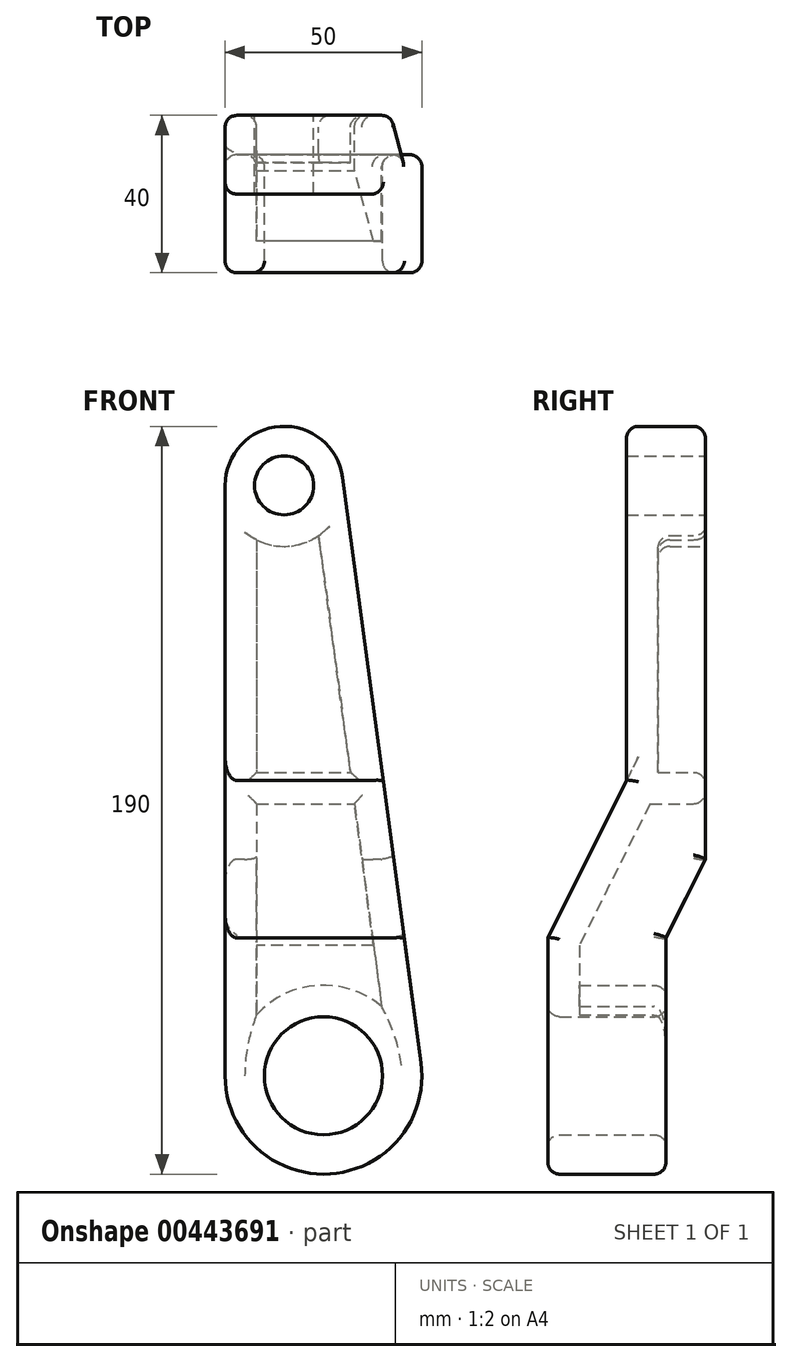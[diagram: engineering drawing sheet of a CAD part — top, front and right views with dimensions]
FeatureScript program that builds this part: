
annotation { "Feature Type Name" : "Feature", "Feature Type Description" : "" }
export const myFeature = defineFeature(function(context is Context, id is Id, definition is map)
    precondition{}
    {
        {
            var Q0;
            Q0=qCreatedBy(makeId("Front.planeOp"),FACE);
            var sketch = newSketch(context, id + "F0", { "sketchPlane" : qUnion([Q0])});
            skCircle(sketch, "E0", {"center": v(0, 0) * mm, "radius": 25 * mm});
            skCircle(sketch, "E1", {"center": v(-10, 150) * mm, "radius": 15 * mm});
            skLineSegment(sketch, "E2", {"start": v(-25, 150) * mm, "end": v(-25, 0) * mm});
            skLineSegment(sketch, "E3", {"start": v(4.87, 152) * mm, "end": v(24.78, 3.32) * mm});
            skSolve(sketch);
        }
        {
            var Q0;
            Q0 = qSketchRegion(id + "F0", true);
            extrude(context, id + "F1", {"entities" : qUnion([Q0]), "depth" : 40 * mm});
        }
        {
            var Q0;
            Q0=makeQuery(id+"F1.opExtrude","SWEPT_FACE",FACE,{"disambiguationData":[OSD([sQuery(id+"F0.wireOp",EDGE,"E2")])]});
            var sketch = newSketch(context, id + "F2", { "sketchPlane" : qUnion([Q0])});
            skLineSegment(sketch, "E4", {"start": v(0, 0) * mm, "end": v(0, -25.94) * mm});
            skLineSegment(sketch, "E5", {"start": v(10, -25.94) * mm, "end": v(10, 35) * mm});
            skLineSegment(sketch, "E6", {"start": v(10, 35) * mm, "end": v(0, 55) * mm});
            skLineSegment(sketch, "E7", {"start": v(0, 55) * mm, "end": v(0, -25.94) * mm});
            skLineSegment(sketch, "E8", {"start": v(40, 35) * mm, "end": v(40, 165.97) * mm});
            skLineSegment(sketch, "E9", {"start": v(20, 165.97) * mm, "end": v(20, 75) * mm});
            skLineSegment(sketch, "E10", {"start": v(20, 75) * mm, "end": v(40, 35) * mm});
            skLineSegment(sketch, "E11", {"start": v(0, -25.94) * mm, "end": v(10, -25.94) * mm});
            skLineSegment(sketch, "E12", {"start": v(20, 165.97) * mm, "end": v(40, 165.97) * mm});
            skSolve(sketch);
        }
        {
            var Q0;
            Q0 = qSketchRegion(id + "F2", true);
            extrude(context, id + "F3", {"entities" : qUnion([Q0]), "operationType" : NewBodyOperationType.REMOVE, "endBound" : BoundingType.THROUGH_ALL, "oppositeDirection" : true, "depth" : 25 * mm});
        }
        {
            var Q0;
            Q0=makeQuery(id+"F1.opExtrude","CAP_FACE",FACE,{"disambiguationData":[OSD([sQuery(id+"F0.wireOp",EDGE,"E0"),sQuery(id+"F0.wireOp",EDGE,"E1"),sQuery(id+"F0.wireOp",EDGE,"E2"),sQuery(id+"F0.wireOp",EDGE,"E3")])],"isStart":true});
            var sketch = newSketch(context, id + "F4", { "sketchPlane" : qUnion([Q0])});
            skCircle(sketch, "E13", {"center": v(10, 150) * mm, "radius": 7.5 * mm});
            skCircle(sketch, "E14", {"center": v(0, 0) * mm, "radius": 15 * mm});
            skSolve(sketch);
        }
        {
            var Q0;
            Q0 = qSketchRegion(id + "F4", true);
            extrude(context, id + "F5", {"entities" : qUnion([Q0]), "operationType" : NewBodyOperationType.REMOVE, "endBound" : BoundingType.THROUGH_ALL, "oppositeDirection" : true, "depth" : 25 * mm});
        }
        {
            var Q0;
            Q0=makeQuery(id+"F1.opExtrude","CAP_FACE",FACE,{"disambiguationData":[OSD([sQuery(id+"F0.wireOp",EDGE,"E0"),sQuery(id+"F0.wireOp",EDGE,"E1"),sQuery(id+"F0.wireOp",EDGE,"E2"),sQuery(id+"F0.wireOp",EDGE,"E3")])],"isStart":true});
            var Q1;
            Q1=makeQuery(id+"F3.boolean.opBoolean","COPY",FACE,{"derivedFrom":makeQuery(id+"F3.opExtrude","SWEPT_FACE",FACE,{"disambiguationData":[OSD([sQuery(id+"F2.wireOp",EDGE,"E6")])]})});
            var Q2;
            Q2=makeQuery(id+"F3.boolean.opBoolean","COPY",FACE,{"derivedFrom":makeQuery(id+"F3.opExtrude","SWEPT_FACE",FACE,{"disambiguationData":[OSD([sQuery(id+"F2.wireOp",EDGE,"E5")])]})});
            shell(context, id + "F6", {"entities" : qUnion([Q0, Q1, Q2]), "thickness" : 8 * mm});
        }
        {
            var Q0;
            Q0=makeQuery(id+"F1.opExtrude","CAP_FACE",FACE,{"disambiguationData":[OSD([sQuery(id+"F0.wireOp",EDGE,"E0"),sQuery(id+"F0.wireOp",EDGE,"E1"),sQuery(id+"F0.wireOp",EDGE,"E2"),sQuery(id+"F0.wireOp",EDGE,"E3")])],"isStart":true});
            var sketch = newSketch(context, id + "F7", { "sketchPlane" : qUnion([Q0])});
            skLineSegment(sketch, "E15", {"start": v(-6.82, 77.11) * mm, "end": v(17, 77.11) * mm});
            skLineSegment(sketch, "E16", {"start": v(-7.9, 69.11) * mm, "end": v(17, 69.11) * mm});
            skLineSegment(sketch, "E17.0", {"start": v(-6.82, 77.11) * mm, "end": v(-7.9, 69.11) * mm});
            skLineSegment(sketch, "E18.0", {"start": v(17, 77.11) * mm, "end": v(17, 69.11) * mm});
            skPoint(sketch, "E19.orphan", {"position": v(1.23, 137.22) * mm});
            skPoint(sketch, "E20.orphan", {"position": v(-9.79, 55) * mm});
            skPoint(sketch, "E21.orphan", {"position": v(17, 55) * mm});
            skPoint(sketch, "E22.orphan", {"position": v(17, 136.17) * mm});
            skSolve(sketch);
        }
        {
            var Q0;
            Q0 = qSketchRegion(id + "F7", true);
            extrude(context, id + "F8", {"entities" : qUnion([Q0]), "operationType" : NewBodyOperationType.ADD, "endBound" : BoundingType.UP_TO_NEXT, "oppositeDirection" : true, "depth" : 25 * mm});
        }
        {
            var Q0;
            Q0=makeQuery(id+"F5.boolean.opBoolean","COPY",EDGE,{"derivedFrom":makeQuery(id+"F5.opExtrude","CAP_EDGE",EDGE,{"disambiguationData":[OSD([sQuery(id+"F4.wireOp",EDGE,"E13")])],"isStart":true})});
            var Q1;
            Q1=makeQuery(id+"F1.opExtrude","CAP_EDGE",EDGE,{"disambiguationData":[OSD([sQuery(id+"F0.wireOp",EDGE,"E1")])],"isStart":true});
            var Q2;
            Q2=makeQuery(id+"F3.boolean.opBoolean","INTERSECT",EDGE,{"derivedFrom":[makeQuery(id+"F1.opExtrude","SWEPT_FACE",FACE,{"disambiguationData":[OSD([sQuery(id+"F0.wireOp",EDGE,"E1")])]}),makeQuery(id+"F3.opExtrude","SWEPT_FACE",FACE,{"disambiguationData":[OSD([sQuery(id+"F2.wireOp",EDGE,"E9")])]})]});
            var Q3;
            Q3=makeQuery(id+"F1.opExtrude","CAP_EDGE",EDGE,{"disambiguationData":[OSD([sQuery(id+"F0.wireOp",EDGE,"E2")])],"isStart":true});
            var Q4;
            Q4=makeQuery(id+"F5.boolean.opBoolean","INTERSECT",EDGE,{"derivedFrom":[makeQuery(id+"F3.boolean.opBoolean","COPY",FACE,{"derivedFrom":makeQuery(id+"F3.opExtrude","SWEPT_FACE",FACE,{"disambiguationData":[OSD([sQuery(id+"F2.wireOp",EDGE,"E5")])]})}),makeQuery(id+"F5.opExtrude","SWEPT_FACE",FACE,{"disambiguationData":[OSD([sQuery(id+"F4.wireOp",EDGE,"E14")])]})]});
            var Q5;
            Q5=makeQuery(id+"F3.boolean.opBoolean","INTERSECT",EDGE,{"derivedFrom":[makeQuery(id+"F1.opExtrude","SWEPT_FACE",FACE,{"disambiguationData":[OSD([sQuery(id+"F0.wireOp",EDGE,"E0")])]}),makeQuery(id+"F3.opExtrude","SWEPT_FACE",FACE,{"disambiguationData":[OSD([sQuery(id+"F2.wireOp",EDGE,"E5")])]})]});
            var Q6;
            Q6=makeQuery(id+"F6.opShell","OFFSET_EDGE",EDGE,{"disambiguationData":[OSD([sQuery(id+"F0.wireOp",EDGE,"E3"),sQuery(id+"F2.wireOp",EDGE,"E5")])]});
            var Q7;
            Q7=makeQuery(id+"F8.opExtrude","CAP_EDGE",EDGE,{"disambiguationData":[OSD([sQuery(id+"F7.wireOp",EDGE,"E16")])],"isStart":true});
            var Q8;
            Q8=makeQuery(id+"F6.opShell","OFFSET_EDGE",EDGE,{"disambiguationData":[OSD([sQuery(id+"F2.wireOp",EDGE,"E6")])]});
            var Q9;
            Q9=makeQuery(id+"F6.opShell","OFFSET_EDGE",EDGE,{"disambiguationData":[OSD([sQuery(id+"F2.wireOp",EDGE,"E5")])]});
            var Q10;
            Q10=makeQuery(id+"F6.opShell","OFFSET_EDGE",EDGE,{"disambiguationData":[OSD([sQuery(id+"F2.wireOp",EDGE,"E5"),sQuery(id+"F4.wireOp",EDGE,"E14")])]});
            var Q11;
            {var subQ0=sQuery(id+"F0.wireOp",EDGE,"E2");Q11=makeQuery(id+"F8.boolean.opBoolean","SPLIT",EDGE,{"disambiguationData":[TD([makeQuery(id+"F3.boolean.opBoolean","COPY",FACE,{"derivedFrom":makeQuery(id+"F3.opExtrude","SWEPT_FACE",FACE,{"disambiguationData":[OSD([sQuery(id+"F2.wireOp",EDGE,"E6")])]})})])],"derivedFrom":makeQuery(id+"F6.opShell","OFFSET_EDGE",EDGE,{"disambiguationData":[OSD([subQ0]),TDD([makeQuery(id+"F1.opExtrude","CAP_EDGE",EDGE,{"disambiguationData":[OSD([subQ0])],"isStart":true})])]})});}
            var Q12;
            {var subQ1=sQuery(id+"F0.wireOp",EDGE,"E3");Q12=makeQuery(id+"F8.boolean.opBoolean","SPLIT",EDGE,{"disambiguationData":[TD([makeQuery(id+"F6.opShell","OFFSET_FACE",FACE,{"disambiguationData":[OSD([sQuery(id+"F2.wireOp",EDGE,"E6")])]})])],"derivedFrom":makeQuery(id+"F6.opShell","OFFSET_EDGE",EDGE,{"disambiguationData":[OSD([subQ1]),TDD([makeQuery(id+"F1.opExtrude","CAP_EDGE",EDGE,{"disambiguationData":[OSD([subQ1])],"isStart":true})])]})});}
            var Q13;
            Q13=makeQuery(id+"F6.opShell","OFFSET_EDGE",EDGE,{"disambiguationData":[OSD([sQuery(id+"F0.wireOp",EDGE,"E3"),sQuery(id+"F2.wireOp",EDGE,"E6")])]});
            var Q14;
            {var subQ1=sQuery(id+"F0.wireOp",EDGE,"E3");Q14=makeQuery(id+"F8.boolean.opBoolean","SPLIT",EDGE,{"disambiguationData":[TD([makeQuery(id+"F6.opShell","OFFSET_FACE",FACE,{"disambiguationData":[OSD([sQuery(id+"F4.wireOp",EDGE,"E13")])]})])],"derivedFrom":makeQuery(id+"F6.opShell","OFFSET_EDGE",EDGE,{"disambiguationData":[OSD([subQ1]),TDD([makeQuery(id+"F1.opExtrude","CAP_EDGE",EDGE,{"disambiguationData":[OSD([subQ1])],"isStart":true})])]})});}
            var Q15;
            Q15=makeQuery(id+"F6.opShell","OFFSET_EDGE",EDGE,{"disambiguationData":[OSD([sQuery(id+"F4.wireOp",EDGE,"E13")])]});
            var Q16;
            {var subQ1=sQuery(id+"F0.wireOp",EDGE,"E2");Q16=makeQuery(id+"F8.boolean.opBoolean","SPLIT",EDGE,{"disambiguationData":[TD([makeQuery(id+"F6.opShell","OFFSET_FACE",FACE,{"disambiguationData":[OSD([sQuery(id+"F4.wireOp",EDGE,"E13")])]})])],"derivedFrom":makeQuery(id+"F6.opShell","OFFSET_EDGE",EDGE,{"disambiguationData":[OSD([subQ1]),TDD([makeQuery(id+"F1.opExtrude","CAP_EDGE",EDGE,{"disambiguationData":[OSD([subQ1])],"isStart":true})])]})});}
            var Q17;
            Q17=makeQuery(id+"F1.opExtrude","CAP_EDGE",EDGE,{"disambiguationData":[OSD([sQuery(id+"F0.wireOp",EDGE,"E3")])],"isStart":true});
            var Q18;
            Q18=makeQuery(id+"F3.boolean.opBoolean","INTERSECT",EDGE,{"derivedFrom":[makeQuery(id+"F1.opExtrude","SWEPT_FACE",FACE,{"disambiguationData":[OSD([sQuery(id+"F0.wireOp",EDGE,"E3")])]}),makeQuery(id+"F3.opExtrude","SWEPT_FACE",FACE,{"disambiguationData":[OSD([sQuery(id+"F2.wireOp",EDGE,"E9")])]})]});
            var Q19;
            Q19=makeQuery(id+"F3.boolean.opBoolean","INTERSECT",EDGE,{"derivedFrom":[makeQuery(id+"F1.opExtrude","SWEPT_FACE",FACE,{"disambiguationData":[OSD([sQuery(id+"F0.wireOp",EDGE,"E3")])]}),makeQuery(id+"F3.opExtrude","SWEPT_FACE",FACE,{"disambiguationData":[OSD([sQuery(id+"F2.wireOp",EDGE,"E10")])]})]});
            var Q20;
            Q20=makeQuery(id+"F1.opExtrude","CAP_EDGE",EDGE,{"disambiguationData":[OSD([sQuery(id+"F0.wireOp",EDGE,"E3")])],"isStart":false});
            var Q21;
            Q21=makeQuery(id+"F1.opExtrude","CAP_EDGE",EDGE,{"disambiguationData":[OSD([sQuery(id+"F0.wireOp",EDGE,"E0")])],"isStart":false});
            var Q22;
            Q22=makeQuery(id+"F3.boolean.opBoolean","COPY",EDGE,{"derivedFrom":makeQuery(id+"F3.opExtrude","CAP_EDGE",EDGE,{"disambiguationData":[OSD([sQuery(id+"F2.wireOp",EDGE,"E10")])],"isStart":true})});
            var Q23;
            Q23=makeQuery(id+"F1.opExtrude","CAP_EDGE",EDGE,{"disambiguationData":[OSD([sQuery(id+"F0.wireOp",EDGE,"E2")])],"isStart":false});
            var Q24;
            Q24=makeQuery(id+"F5.boolean.opBoolean","INTERSECT",EDGE,{"derivedFrom":[makeQuery(id+"F1.opExtrude","CAP_FACE",FACE,{"disambiguationData":[OSD([sQuery(id+"F0.wireOp",EDGE,"E0"),sQuery(id+"F0.wireOp",EDGE,"E1"),sQuery(id+"F0.wireOp",EDGE,"E2"),sQuery(id+"F0.wireOp",EDGE,"E3")])],"isStart":false}),makeQuery(id+"F5.opExtrude","SWEPT_FACE",FACE,{"disambiguationData":[OSD([sQuery(id+"F4.wireOp",EDGE,"E14")])]})]});
            var Q25;
            Q25=makeQuery(id+"F3.boolean.opBoolean","INTERSECT",EDGE,{"derivedFrom":[makeQuery(id+"F1.opExtrude","SWEPT_FACE",FACE,{"disambiguationData":[OSD([sQuery(id+"F0.wireOp",EDGE,"E3")])]}),makeQuery(id+"F3.opExtrude","SWEPT_FACE",FACE,{"disambiguationData":[OSD([sQuery(id+"F2.wireOp",EDGE,"E6")])]})]});
            var Q26;
            Q26=makeQuery(id+"F3.boolean.opBoolean","INTERSECT",EDGE,{"derivedFrom":[makeQuery(id+"F1.opExtrude","SWEPT_FACE",FACE,{"disambiguationData":[OSD([sQuery(id+"F0.wireOp",EDGE,"E3")])]}),makeQuery(id+"F3.opExtrude","SWEPT_FACE",FACE,{"disambiguationData":[OSD([sQuery(id+"F2.wireOp",EDGE,"E5")])]})]});
            var Q27;
            Q27=makeQuery(id+"F3.boolean.opBoolean","COPY",EDGE,{"derivedFrom":makeQuery(id+"F3.opExtrude","CAP_EDGE",EDGE,{"disambiguationData":[OSD([sQuery(id+"F2.wireOp",EDGE,"E6")])],"isStart":true})});
            var Q28;
            Q28=makeQuery(id+"F3.boolean.opBoolean","COPY",EDGE,{"derivedFrom":makeQuery(id+"F3.opExtrude","CAP_EDGE",EDGE,{"disambiguationData":[OSD([sQuery(id+"F2.wireOp",EDGE,"E5")])],"isStart":true})});
            var Q29;
            Q29=makeQuery(id+"F8.opExtrude","CAP_EDGE",EDGE,{"disambiguationData":[OSD([sQuery(id+"F7.wireOp",EDGE,"E15")])],"isStart":true});
            var Q30;
            Q30=makeQuery(id+"F3.boolean.opBoolean","COPY",EDGE,{"derivedFrom":makeQuery(id+"F3.opExtrude","CAP_EDGE",EDGE,{"disambiguationData":[OSD([sQuery(id+"F2.wireOp",EDGE,"E9")])],"isStart":true})});
            fillet(context, id + "F9", {"entities" : qUnion([Q0, Q1, Q2, Q3, Q4, Q5, Q6, Q7, Q8, Q9, Q10, Q11, Q12, Q13, Q14, Q15, Q16, Q17, Q18, Q19, Q20, Q21, Q22, Q23, Q24, Q25, Q26, Q27, Q28, Q29, Q30]), "radius" : 3 * mm, "tangentPropagation" : true, "allowEdgeOverflow" : false});
        }
    });
